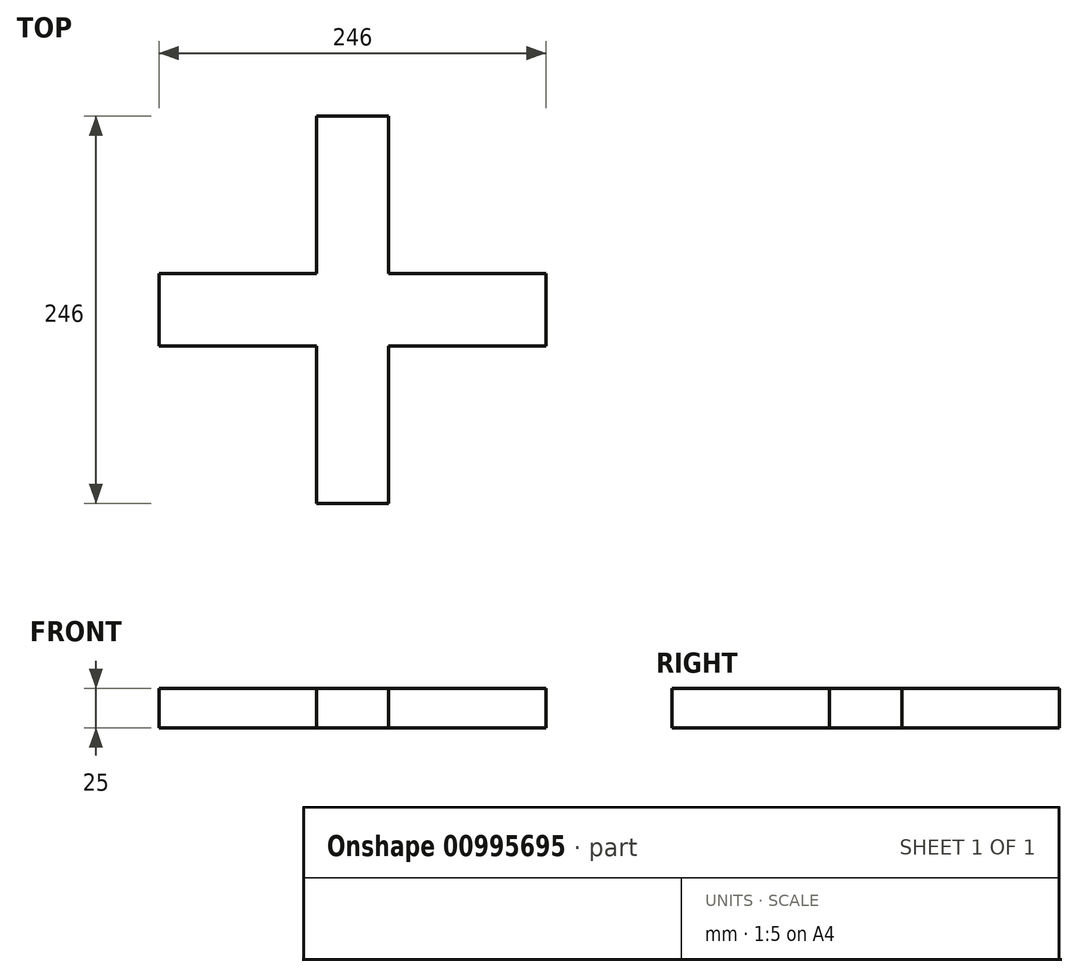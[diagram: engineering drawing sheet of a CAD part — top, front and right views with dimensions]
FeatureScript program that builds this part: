
annotation { "Feature Type Name" : "Feature", "Feature Type Description" : "" }
export const myFeature = defineFeature(function(context is Context, id is Id, definition is map)
    precondition{}
    {
        {
            var Q0;
            Q0=qCreatedBy(makeId("Top.planeOp"),FACE);
            var sketch = newSketch(context, id + "F0", { "sketchPlane" : qUnion([Q0])});
            skLineSegment(sketch, "E0", {"start": v(-31.58, -146) * mm, "end": v(-77.58, -146) * mm});
            skLineSegment(sketch, "E1", {"start": v(-77.58, -146) * mm, "end": v(-77.58, -46) * mm});
            skLineSegment(sketch, "E2", {"start": v(-77.58, -46) * mm, "end": v(-177.58, -46) * mm});
            skLineSegment(sketch, "E3", {"start": v(-177.58, -46) * mm, "end": v(-177.58, 0) * mm});
            skLineSegment(sketch, "E4", {"start": v(-177.58, 0) * mm, "end": v(-77.58, 0) * mm});
            skLineSegment(sketch, "E5", {"start": v(-77.58, 0) * mm, "end": v(-77.58, 100) * mm});
            skLineSegment(sketch, "E6", {"start": v(-77.58, 100) * mm, "end": v(-31.58, 100) * mm});
            skLineSegment(sketch, "E7", {"start": v(-31.58, 100) * mm, "end": v(-31.58, 0) * mm});
            skLineSegment(sketch, "E8", {"start": v(-31.58, 0) * mm, "end": v(68.42, 0) * mm});
            skLineSegment(sketch, "E9", {"start": v(68.42, 0) * mm, "end": v(68.42, -46) * mm});
            skLineSegment(sketch, "E10", {"start": v(68.42, -46) * mm, "end": v(-31.58, -46) * mm});
            skLineSegment(sketch, "E11", {"start": v(-31.58, -46) * mm, "end": v(-31.58, -146) * mm});
            skSolve(sketch);
        }
        {
            var Q0;
            Q0=makeQuery(id+"F0.imprint","IMPRINT",FACE,{"disambiguationData":[TD([[makeQuery(id+"F0.imprint","IMPRINT",EDGE,{"derivedFrom":sQuery(id+"F0.wireOp",EDGE,"E0")}),-1.0]])]});
            extrude(context, id + "F1", {"entities" : qUnion([Q0]), "depth" : 25 * mm, "offsetDistance" : 25 * mm});
        }
    });
